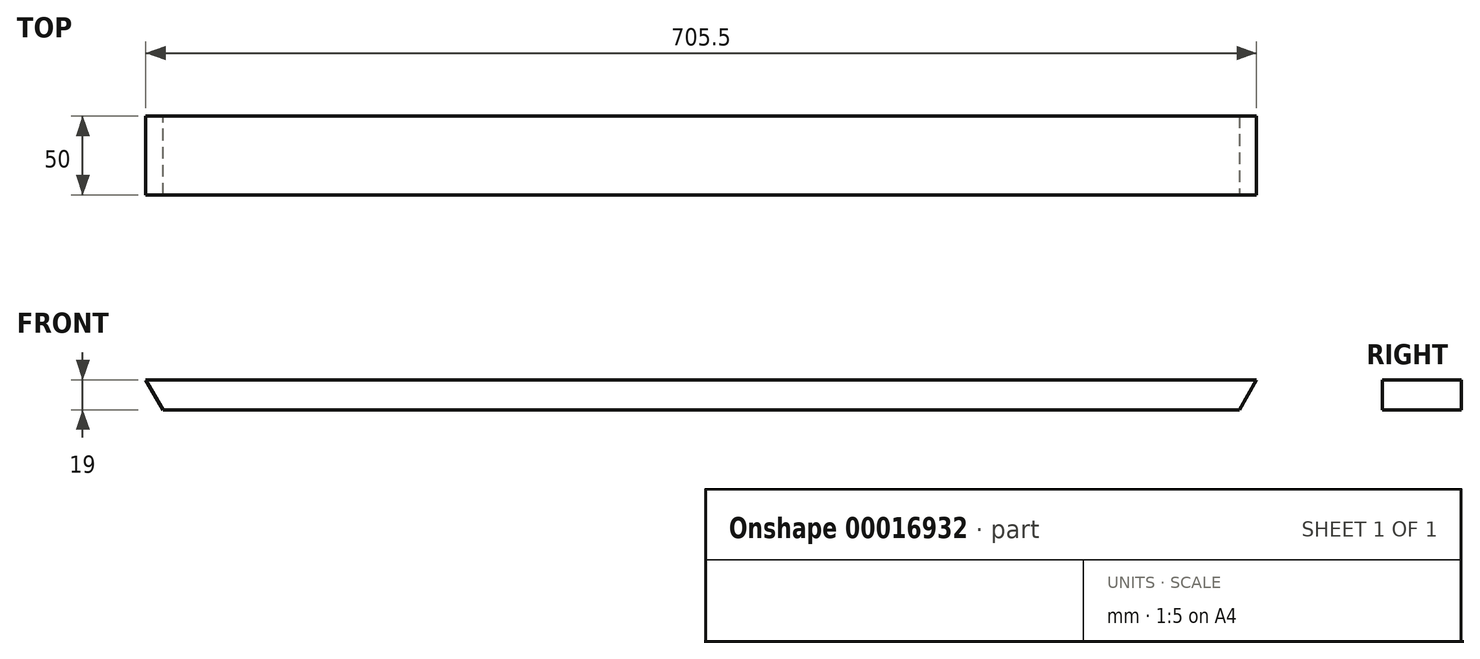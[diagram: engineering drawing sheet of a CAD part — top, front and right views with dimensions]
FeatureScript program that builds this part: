
annotation { "Feature Type Name" : "Feature", "Feature Type Description" : "" }
export const myFeature = defineFeature(function(context is Context, id is Id, definition is map)
    precondition{}
    {
        {
            var Q0;
            Q0=qCreatedBy(makeId("Front.planeOp"),FACE);
            var sketch = newSketch(context, id + "F0", { "sketchPlane" : qUnion([Q0])});
            skLineSegment(sketch, "E0.rect.bottom", {"start": v(352.75, -9.5) * mm, "end": v(-352.75, -9.5) * mm});
            skPoint(sketch, "E0.rect.middle", {"position": v(0, 0) * mm});
            skLineSegment(sketch, "E0.rect.top", {"start": v(352.75, 9.5) * mm, "end": v(-352.75, 9.5) * mm});
            skLineSegment(sketch, "E0.rect.left", {"start": v(352.75, -9.5) * mm, "end": v(352.75, 9.5) * mm});
            skLineSegment(sketch, "E0.rect.right", {"start": v(-352.75, -9.5) * mm, "end": v(-352.75, 9.5) * mm});
            skSolve(sketch);
        }
        {
            var Q0;
            Q0=qSketchRegion(id+"F0",true);
            extrude(context, id + "F1", {"entities" : qUnion([Q0]), "depth" : 50 * mm});
        }
        {
            var Q0;
            Q0=makeQuery(id+"F1.opExtrude","SWEPT_EDGE",EDGE,{"disambiguationData":[OSD([sQuery(id+"F0.wireOp",EDGE,"E0.rect.bottom"),sQuery(id+"F0.wireOp",EDGE,"E0.rect.right")])]});
            var Q1;
            Q1=makeQuery(id+"F1.opExtrude","SWEPT_EDGE",EDGE,{"disambiguationData":[OSD([sQuery(id+"F0.wireOp",EDGE,"E0.rect.bottom"),sQuery(id+"F0.wireOp",EDGE,"E0.rect.left")])]});
            chamfer(context, id + "F2", {"entities" : qUnion([Q0, Q1]), "chamferType" : ChamferType.OFFSET_ANGLE, "width" : 19 * mm, "oppositeDirection" : true, "angle" : 30 * degree, "tangentPropagation" : true});
        }
    });
